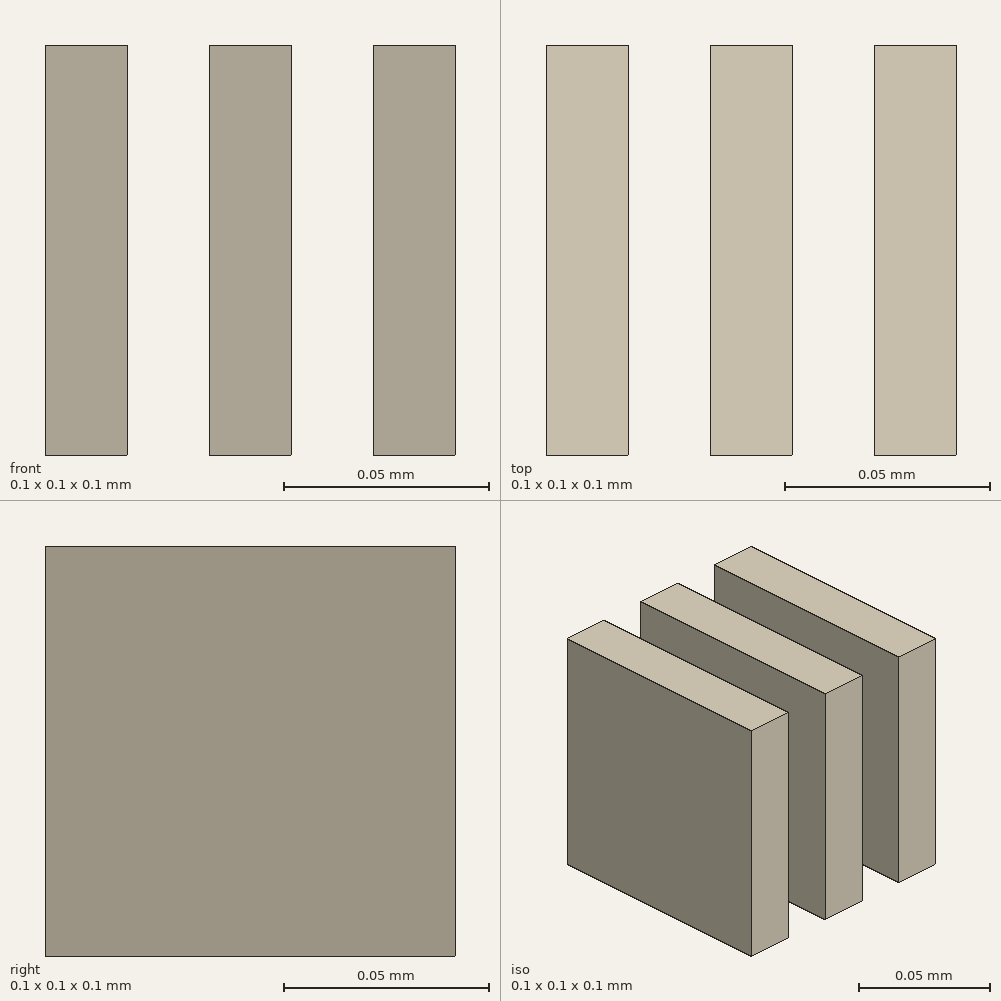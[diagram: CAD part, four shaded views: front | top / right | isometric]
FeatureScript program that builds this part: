
annotation { "Feature Type Name" : "Feature", "Feature Type Description" : "" }
export const myFeature = defineFeature(function(context is Context, id is Id, definition is map)
    precondition{}
    {
        {
            var Q0;
            Q0=qCreatedBy(makeId("Top.planeOp"),FACE);
            var sketch = newSketch(context, id + "F0", { "sketchPlane" : qUnion([Q0])});
            skLineSegment(sketch, "E0.bottom", {"start": v(0, 0) * mm, "end": v(0.02, 0) * mm});
            skLineSegment(sketch, "E0.top", {"start": v(0, -0.1) * mm, "end": v(0.02, -0.1) * mm});
            skLineSegment(sketch, "E0.left", {"start": v(0, 0) * mm, "end": v(0, -0.1) * mm});
            skLineSegment(sketch, "E0.right", {"start": v(0.1, 0) * mm, "end": v(0.1, -0.1) * mm});
            skLineSegment(sketch, "E1.0", {"start": v(0.02, 0) * mm, "end": v(0.02, -0.1) * mm});
            skLineSegment(sketch, "E2.0", {"start": v(0.08, 0) * mm, "end": v(0.08, -0.1) * mm});
            skLineSegment(sketch, "E3.0", {"start": v(0.06, 0) * mm, "end": v(0.06, -0.1) * mm});
            skLineSegment(sketch, "E4.0", {"start": v(0.04, 0) * mm, "end": v(0.04, -0.1) * mm});
            skLineSegment(sketch, "E5.trimOffspring", {"start": v(0.04, 0) * mm, "end": v(0.06, 0) * mm});
            skLineSegment(sketch, "E6.trimOffspring", {"start": v(0.08, 0) * mm, "end": v(0.1, 0) * mm});
            skLineSegment(sketch, "E7.trimOffspring", {"start": v(0.08, -0.1) * mm, "end": v(0.1, -0.1) * mm});
            skLineSegment(sketch, "E8.trimOffspring", {"start": v(0.04, -0.1) * mm, "end": v(0.06, -0.1) * mm});
            skSolve(sketch);
        }
        {
            var Q0;
            Q0=makeQuery(id+"F0.imprint","IMPRINT",FACE,{"disambiguationData":[TD([[makeQuery(id+"F0.imprint","IMPRINT",EDGE,{"derivedFrom":sQuery(id+"F0.wireOp",EDGE,"E0.top")}),1.0]])]});
            var Q1;
            Q1=makeQuery(id+"F0.imprint","IMPRINT",FACE,{"disambiguationData":[TD([[makeQuery(id+"F0.imprint","IMPRINT",EDGE,{"derivedFrom":sQuery(id+"F0.wireOp",EDGE,"E3.0")}),-1.0]])]});
            var Q2;
            Q2=makeQuery(id+"F0.imprint","IMPRINT",FACE,{"disambiguationData":[TD([[makeQuery(id+"F0.imprint","IMPRINT",EDGE,{"derivedFrom":sQuery(id+"F0.wireOp",EDGE,"E0.right")}),-1.0]])]});
            extrude(context, id + "F1", {"entities" : qUnion([Q0, Q1, Q2]), "depth" : .1 * mm, "offsetDistance" : 25 * mm});
        }
    });
